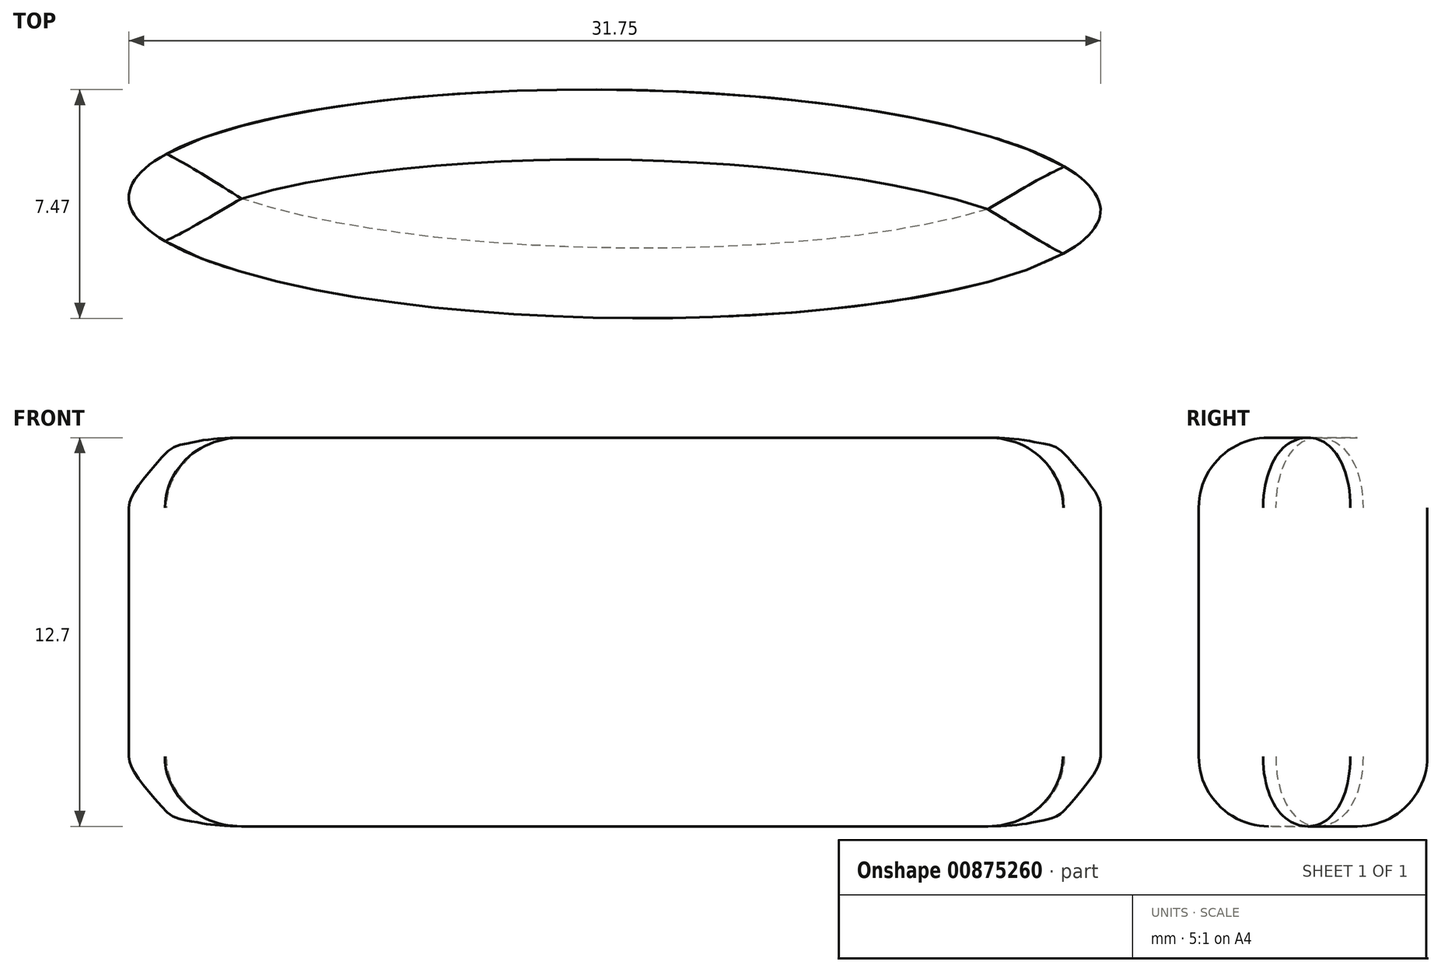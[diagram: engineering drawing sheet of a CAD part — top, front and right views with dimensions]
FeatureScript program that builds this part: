
annotation { "Feature Type Name" : "Feature", "Feature Type Description" : "" }
export const myFeature = defineFeature(function(context is Context, id is Id, definition is map)
    precondition{}
    {
        {
            var Q0;
            Q0=qCreatedBy(makeId("Top.planeOp"),FACE);
            var sketch = newSketch(context, id + "F0", { "sketchPlane" : qUnion([Q0])});
            skEllipse(sketch, "E0", {"center": v(-41.62, 59.63) * mm, "majorRadius": 15.88 * mm, "minorRadius": 3.73 * mm, "majorAxis": v(1, -0.01)});
            skSolve(sketch);
        }
        {
            var Q0;
            Q0 = qSketchRegion(id + "F0", true);
            extrude(context, id + "F1", {"entities" : qUnion([Q0]), "depth" : 12.7 * mm, "offsetDistance" : 25.4 * mm});
        }
        {
            var Q0;
            Q0=makeQuery(id+"F1.opExtrude","CAP_EDGE",EDGE,{"disambiguationData":[OSD([sQuery(id+"F0.wireOp",EDGE,"E0")])],"isStart":false});
            var Q1;
            Q1=makeQuery(id+"F1.opExtrude","CAP_EDGE",EDGE,{"disambiguationData":[OSD([sQuery(id+"F0.wireOp",EDGE,"E0")])],"isStart":true});
            fillet(context, id + "F2", {"entities" : qUnion([Q0, Q1]), "radius" : 2.3 * mm, "tangentPropagation" : true, "allowEdgeOverflow" : false});
        }
    });
